# Revit family: Sanitary_Mirrors_Slits_Mirror
name_source: partatom
category: Furniture
units: mm (PartAtom-declared; Revit-internal decimal feet)

## family parameters
Always vertical = No
Cut with Voids When Loaded = No
OmniClass Number = 23.40.20.00
OmniClass Title = General Furniture and Specialties
Room Calculation Point = No
Shared = No
Work Plane-Based = Yes

## types (1)
- Slits Mirror
    AssetType = Fixed
    BIMObjectName = Sanitary_Mirrors_Slits_Mirror
    Brand = Svedholm
    Color = Various
    Cost = 0 $
    Default Elevation = 1219 mm
    Description = A mirror with powder coated steel frame. All colours are available upon request.
The entire SLITS collection is approved by the Swedish BYGGVARUBEDÖMNINGEN and assessed in SundaHus Material Data.
    DurationUnit = Year
    IfcExportAs = IfcFurnishingElementType
    IfcExportType = MIRROR
    MainColor = White
    Manufacturer = Svedholm
    ManufacturerName = Svedholm
    ManufacturerURL = https://www.svedholm.se
    Material = Metal and mirror
    MirrorMainMaterial = Mirror Glass
    MirrorSecondaryMaterial = RAL 7021
    Model = Slits Mirror
    ModelNumber = 111.100.004
    NBSDescription = Mirrors
    NBSReference = 45-35-72/336
    Name = Slits_Mirror
    NominalDepth = 31 mm
    NominalHeight = 900 mm  [stored 2.95276 ft]
    NominalLength = 600 mm
    ProductInformation = A mirror with powder coated steel frame. All colours are available upon request.
The entire SLITS collection is approved by the Swedish BYGGVARUBEDÖMNINGEN and assessed in SundaHus Material Data.
    Shape = Sculptured
    Size = 900 ×600 ×3 mm
    URL = https://www.svedholm.se
    Uniclass2 = Pr_25_71_53
    Uniclass2015Description = Mirrors
    Uniclass2015Reference = Pr_25_71_53
    Version = 1
    VersionDate = 06/07/2023
    WarrantyDurationUnit = Years

note: [stored X ft] marks values corroborated as IEEE doubles in the binary element streams (Revit-internal decimal feet)

## geometry (parser evidence)
native form markers: Sweep x6
no freeform markers — native parametric forms only
